# Revit family: 1SE_Trez_TC_T_1500_With_Pit
name_source: partatom
category: Specialty Equipment
units: mm (PartAtom-declared; Revit-internal decimal feet)

## family parameters
Always vertical = Yes
Cut with Voids When Loaded = Yes
Part Type = Normal
Room Calculation Point = No
Round Connector Dimension = Use Diameter
Shared = No
Work Plane-Based = No

## types (1)
- Platform-1700x1300mm with Door Height 2500mm
    A-Side = No
    B-Side = Yes
    C-Side = Yes
    Cabin = Speciality_Equipment_Trez_Cabin_Sgl_C : Cabin
    Cabin or Platform = Speciality_Equipment_Trez_Platform_Sgl_C : Platform
    Clear Depth = 1300 mm  [stored 4.26509 ft]
    Clear Width = 1700 mm  [stored 5.57743 ft]
    Clearance = 425 mm  [stored 1.39436 ft]
    D-Side = Yes
    Description = TC T is the best choice when the budget is small, but the safety requirements are high. TC T is not fixed forever to the building. It can be installed directly on the ground floor and later dismounted and installed in another place. The TC T complies with the machinery directive 2006/42/EC. From the menu below, you can choose the lift and the tower options to fit perfectly for your project.
    Door Clear Height = 2500 mm  [stored 8.2021 ft]
    Door Clear Width = 1700 mm  [stored 5.57743 ft]
    Headroom = 3100 mm
    Manufacturer = TREZ Ltd.
    Model = TC T 1500
    Pit Height = 150 mm
    Platform = Speciality_Equipment_Trez_Platform_Sgl_C : Platform
    Platform Material = TREZ_Steel
    Profiles Material = TREZ_Steel
    Rail Height = 7750 mm  [stored 25.4265 ft]
    Real Depth = 1300 mm  [stored 4.26509 ft]
    Real Width = 1700 mm  [stored 5.57743 ft]
    Safe Space = 600 mm
    Safe Working Load = 1500.00 kg
    Side Clearance = 105 mm  [stored 0.344488 ft]
    Tower Cladding Material = TREZ_Steel_Cladding
    Tower Depth = 1830 mm
    Tower Width = 1910 mm
    Travel = 4500 mm
    URL = https://trez.bg

note: [stored X ft] marks values corroborated as IEEE doubles in the binary element streams (Revit-internal decimal feet)

## geometry (parser evidence)
native form markers: Sweep x12
no freeform markers — native parametric forms only
